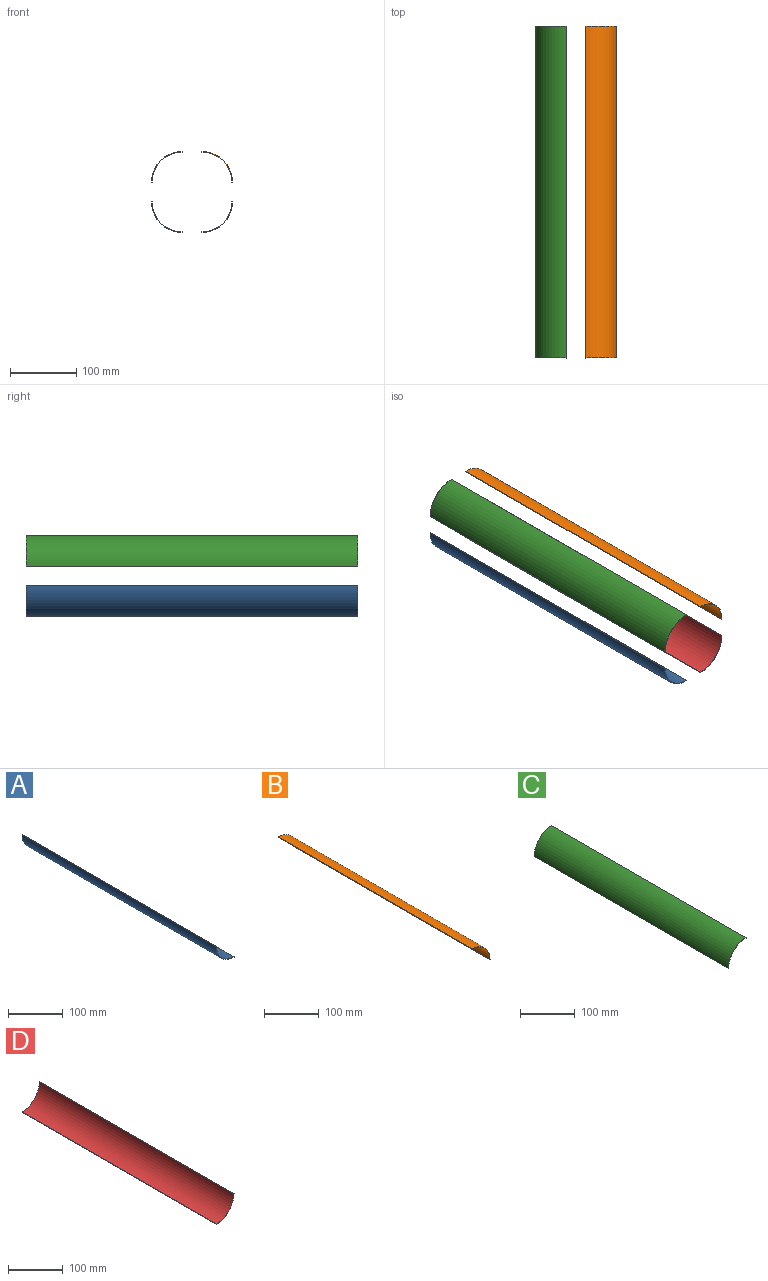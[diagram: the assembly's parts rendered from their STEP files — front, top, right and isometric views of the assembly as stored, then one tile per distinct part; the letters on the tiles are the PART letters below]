
ASSEMBLY  parts=4 mates=3
PART A: 6 faces, bbox 46x500x46 mm
  f0: cylinder r=46mm len=500mm, axis (0,1,0), area 36128.3mm2, adj f2,f3,f4,f5
  f1: cylinder r=45mm len=500mm, axis (0,1,0), area 35342.9mm2, adj f2,f3,f4,f5
  f2: plane 46x46mm, normal (0,-1,0), area 71.5mm2, adj f0,f1,f4,f5
  f3: plane 46x46mm, normal (0,1,0), area 71.5mm2, adj f0,f1,f4,f5
  f4: plane 500x1mm, normal (0,0,1), area 500mm2, adj f0,f1,f2,f3
  f5: plane 500x1mm, normal (1,0,0), area 500mm2, adj f0,f1,f2,f3
PART B: 6 faces, bbox 46x500x46 mm
  f0: plane 500x1mm, normal (0,0,-1), area 500mm2, adj f1,f2,f3,f4
  f1: cylinder r=46mm len=500mm, axis (0,1,0), area 36128.3mm2, adj f0,f3,f4,f5
  f2: cylinder r=45mm len=500mm, axis (0,1,0), area 35342.9mm2, adj f0,f3,f4,f5
  f3: plane 46x46mm, normal (0,-1,0), area 71.5mm2, adj f0,f1,f2,f5
  f4: plane 46x46mm, normal (0,1,0), area 71.5mm2, adj f0,f1,f2,f5
  f5: plane 500x1mm, normal (-1,0,0), area 500mm2, adj f1,f2,f3,f4
PART C: 6 faces, bbox 46x500x46 mm
  f0: plane 46x46mm, normal (0,1,0), area 71.5mm2, adj f2,f3,f4,f5
  f1: plane 46x46mm, normal (0,-1,0), area 71.5mm2, adj f2,f3,f4,f5
  f2: cylinder r=45mm len=500mm, axis (0,1,0), area 35342.9mm2, adj f0,f1,f4,f5
  f3: cylinder r=46mm len=500mm, axis (0,1,0), area 36128.3mm2, adj f0,f1,f4,f5
  f4: plane 500x1mm, normal (0,0,-1), area 500mm2, adj f0,f1,f2,f3
  f5: plane 500x1mm, normal (1,0,0), area 500mm2, adj f0,f1,f2,f3
PART D: 6 faces, bbox 46x500x46 mm
  f0: plane 500x1mm, normal (0,0,1), area 500mm2, adj f1,f2,f3,f4
  f1: plane 46x46mm, normal (0,1,0), area 71.5mm2, adj f0,f3,f4,f5
  f2: plane 46x46mm, normal (0,-1,0), area 71.5mm2, adj f0,f3,f4,f5
  f3: cylinder r=45mm len=500mm, axis (0,1,0), area 35342.9mm2, adj f0,f1,f2,f5
  f4: cylinder r=46mm len=500mm, axis (0,1,0), area 36128.3mm2, adj f0,f1,f2,f5
  f5: plane 500x1mm, normal (-1,0,0), area 500mm2, adj f1,f2,f3,f4
PLACE A t=(-66.98,175.99,-83.01)mm
PLACE B t=(-36.98,175.99,-53.01)mm
PLACE C t=(-66.98,175.99,-53.01)mm
PLACE D t=(-36.98,175.99,-83.01)mm
MATE fastened B.f2 <-> D.f2  axis (0,-1,0) through (-36.98,-324.01,-53.01)mm
MATE fastened B.f1 <-> A.f2  axis (0,-1,0) through (-36.98,-324.01,-53.01)mm
MATE fastened A.f0 <-> C.f1  axis (0,-1,0) through (-66.98,-324.01,-83.01)mm
